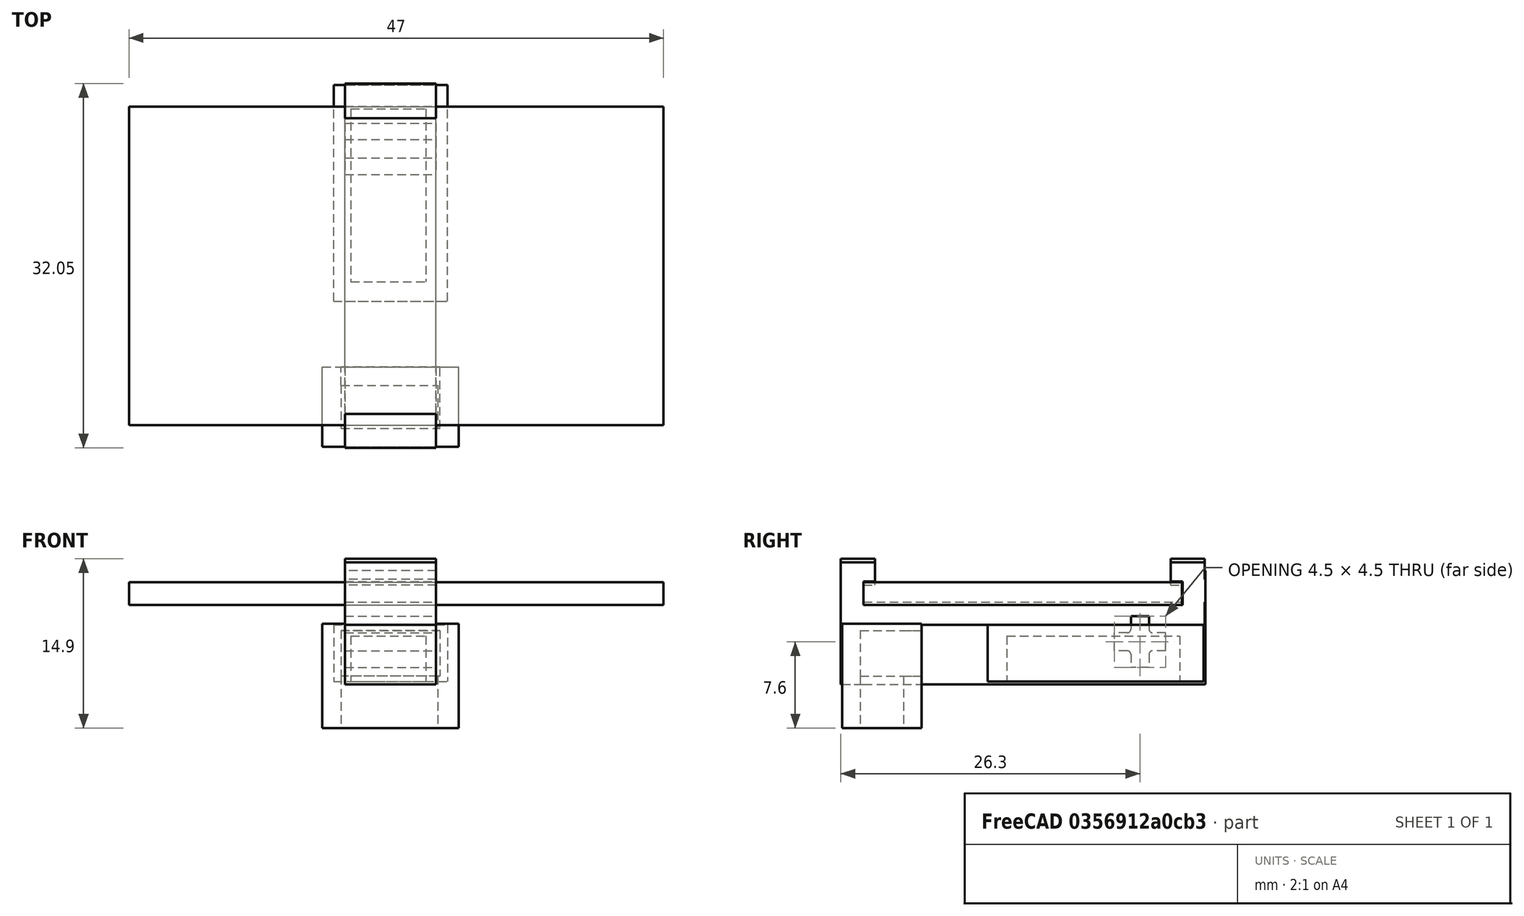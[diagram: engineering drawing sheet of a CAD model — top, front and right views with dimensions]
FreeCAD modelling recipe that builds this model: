
FCSTD DOCUMENT  (FreeCAD 0.20R29177 +426 (Git))
Label: electronicsHolder
License: All rights reserved
LicenseURL: http://en.wikipedia.org/wiki/All_rights_reserved
objects: Part::Box×20, Part::MultiFuse×10, Part::Cut×3, Part::Fillet×1, Mesh::Feature×1
note: 34 computed .brp shape members not serialized (recipe doc carries the construction recipe); baked Part::Feature solids carry a one-line shape summary decoded from their .brp

FEATURE [Part::Box] Box  label="Cube"
  AttacherType = Attacher::AttachEngine3D
  Height = 1.6
  Length = 80
  Placement = pos=(0,-2.25,-0.8) rot=(0,0,1;0rad)
  Width = 4.5
FEATURE [Part::Box] Box001  label="Cube001"
  AttacherType = Attacher::AttachEngine3D
  Height = 1.6
  Length = 80
  Placement = pos=(0,0.8,-2.25) rot=(1,0,0;1.5708rad)
  Width = 4.5
FEATURE [Part::MultiFuse] Fusion
  Placement = pos=(-5,0,0) rot=(0,0,1;0rad)
  Shapes = -> [Box,Box001]
FEATURE [Part::Box] Box002  label="Cube002"
  AttacherType = Attacher::AttachEngine3D
  Height = 7
  Length = 8
  Placement = pos=(0,-3.75,-3.75) rot=(0,0,1;0rad)
  Width = 7.5
FEATURE [Part::Cut] Cut
  Base = -> Box002
  Tool = -> Fusion
FEATURE [Part::Fillet] Fillet
  Base = -> Cut
  Edges = 4 edges r=0.3: [Edge25,Edge30,Edge36,Edge43]
FEATURE [Part::Box] Box003  label="Cube003"
  AttacherType = Attacher::AttachEngine3D
  Height = 10
  Length = 8
  Placement = pos=(0,3.75,-3.75) rot=(0,0,1;0rad)
  Width = 2
FEATURE [Part::Box] Box004  label="bat"
  AttacherType = Attacher::AttachEngine3D
  Height = 2
  Length = 47
  Placement = pos=(-19,-24.3,3.25) rot=(0,0,1;0rad)
  Width = 28
FEATURE [Part::Box] Box005  label="Cube005"
  AttacherType = Attacher::AttachEngine3D
  Height = 2
  Length = 8
  Placement = pos=(0,2.7,5.3) rot=(0,0,1;0rad)
  Width = 3
FEATURE [Part::MultiFuse] Fusion001
  Shapes = -> [Box003,Box005,Fillet]
FEATURE [Part::Box] Box006  label="Cube006"
  AttacherType = Attacher::AttachEngine3D
  Height = 7
  Length = 8
  Placement = pos=(0,-24.3,-3.75) rot=(0,0,1;0rad)
  Width = 21
FEATURE [Part::MultiFuse] Fusion002
  Shapes = -> [Box006,Fusion001]
FEATURE [Part::Box] Box007  label="Cube007"
  AttacherType = Attacher::AttachEngine3D
  Height = 2
  Length = 8
  Placement = pos=(0,-26.3,5.3) rot=(0,0,1;0rad)
  Width = 3
FEATURE [Part::Box] Box008  label="Cube008"
  AttacherType = Attacher::AttachEngine3D
  Height = 10
  Length = 8
  Placement = pos=(0,-26.3,-3.75) rot=(0,0,1;0rad)
  Width = 2
FEATURE [Part::MultiFuse] Fusion003
  Shapes = -> [Box008,Box007]
FEATURE [Part::Box] Box009  label="Cube009"
  AttacherType = Attacher::AttachEngine3D
  Height = 2
  Length = 8
  Placement = pos=(0,3.75,3.5) rot=(0,0,1;0rad)
  Width = 2
FEATURE [Part::Box] Box010  label="Cube010"
  AttacherType = Attacher::AttachEngine3D
  Height = 2
  Length = 8
  Placement = pos=(0,2.7,5) rot=(0,0,1;0rad)
  Width = 3
FEATURE [Part::Box] Box011  label="Cube011"
  AttacherType = Attacher::AttachEngine3D
  Height = 2
  Length = 8
  Placement = pos=(0,-26.3,3.5) rot=(0,0,1;0rad)
  Width = 2
FEATURE [Part::Box] Box012  label="Cube012"
  AttacherType = Attacher::AttachEngine3D
  Height = 2
  Length = 8
  Placement = pos=(0,-26.3,5) rot=(0,0,1;0rad)
  Width = 3
FEATURE [Part::MultiFuse] Fusion005
  Shapes = -> [Box012,Box011]
FEATURE [Part::MultiFuse] Fusion006
  Shapes = -> [Box009,Box010]
FEATURE [Part::Box] Box013  label="Cube013"
  AttacherType = Attacher::AttachEngine3D
  Height = 2
  Length = 8
  Placement = pos=(0,-26.3,1.5) rot=(0,0,1;0rad)
  Width = 32
FEATURE [Part::MultiFuse] Fusion007
  Shapes = -> [Box013,Fusion006,Fusion005]
FEATURE [Part::Box] Box014  label="converter"
  AttacherType = Attacher::AttachEngine3D
  Height = 4.5
  Length = 15.2
  Width = 6.6
FEATURE [Part::Box] Box015  label="Cube014"
  AttacherType = Attacher::AttachEngine3D
  Height = 5
  Length = 19
  Placement = pos=(-1.7,-1.5,-1) rot=(0,0,1;0rad)
  Width = 10
FEATURE [Part::Cut] Cut001
  Base = -> Box015
  Placement = pos=(0.5,-11.7,0.5) rot=(0.707107,0.707107,0;3.14159rad)
  Tool = -> Box014
FEATURE [Part::Box] Box016  label="interruptor"
  AttacherType = Attacher::AttachEngine3D
  Height = 9.3
  Length = 3.8
  Width = 8.5
FEATURE [Part::Box] Box017  label="Cube016"
  AttacherType = Attacher::AttachEngine3D
  Height = 9.2
  Length = 7
  Placement = pos=(-1.6,-1.65,-0.6) rot=(0,0,1;0rad)
  Width = 12
FEATURE [Part::Box] Box018  label="Cube017"
  AttacherType = Attacher::AttachEngine3D
  Height = 4
  Length = 5.8
  Width = 8.7
FEATURE [Part::Box] Box019  label="Cube018"
  AttacherType = Attacher::AttachEngine3D
  Height = 8.5
  Length = 1.6
  Placement = pos=(1.1,2.5,1) rot=(0,0,1;0rad)
  Width = 3.6
FEATURE [Part::MultiFuse] Fusion008
  Shapes = -> [Box016,Box018,Box019]
FEATURE [Part::Cut] Cut002
  Base = -> Box017
  Placement = pos=(-0.35,-24.6,1) rot=(0.707107,0.707107,0;3.14159rad)
  Tool = -> Fusion008
FEATURE [Part::MultiFuse] Fusion004
  Shapes = -> [Fusion003,Fusion002]
FEATURE [Part::MultiFuse] Fusion009
  Shapes = -> [Cut001,Cut002,Fusion007]
FEATURE [Mesh::Feature] Mesh  label="Fusion009 (Meshed)"
